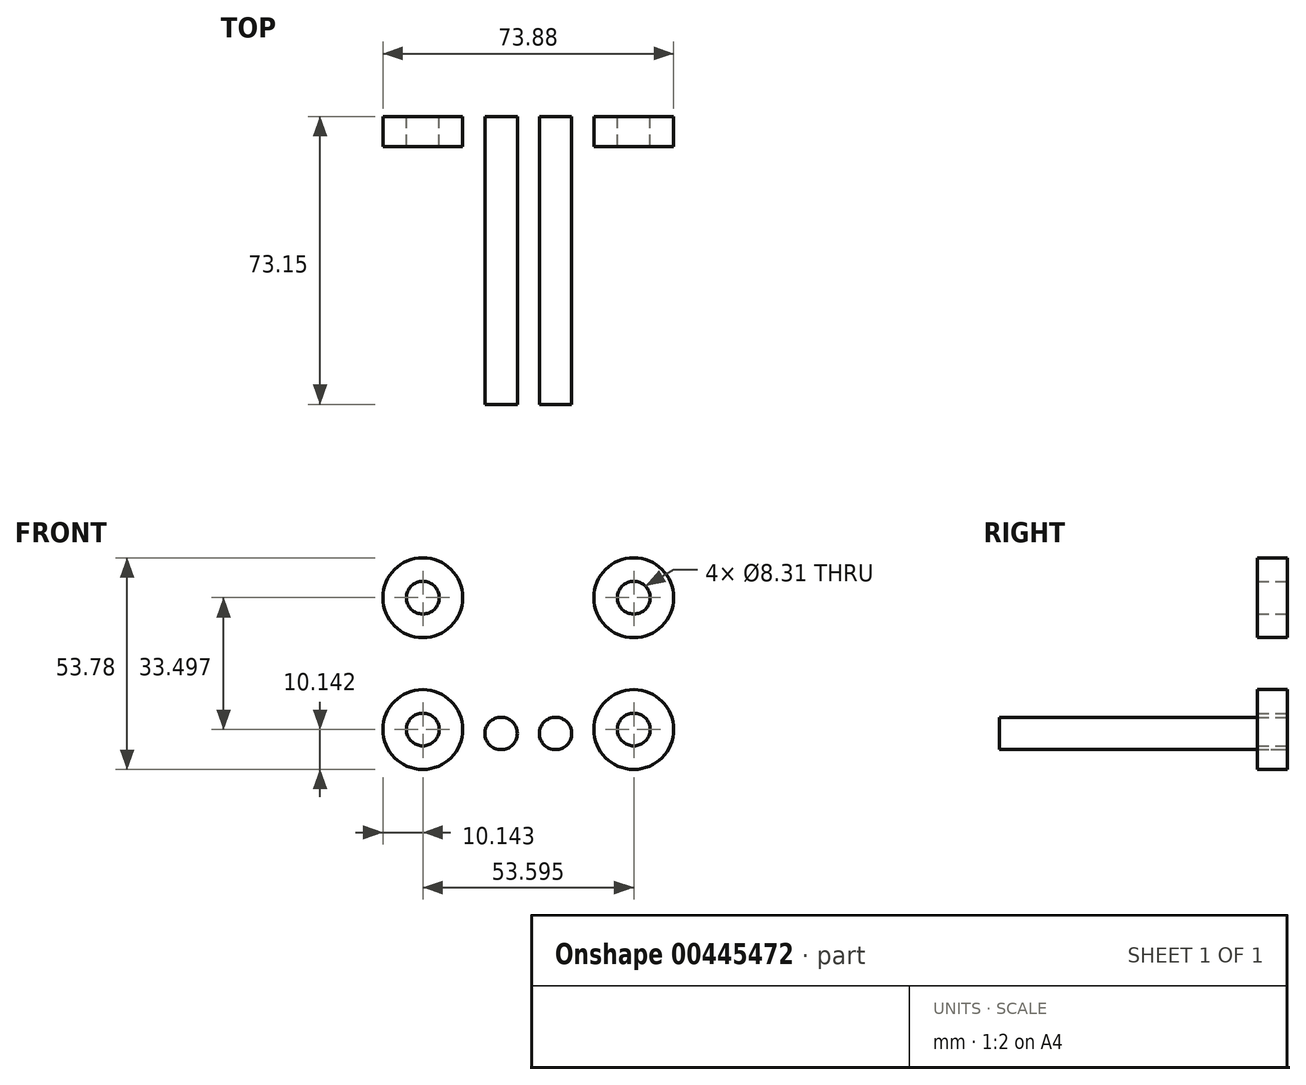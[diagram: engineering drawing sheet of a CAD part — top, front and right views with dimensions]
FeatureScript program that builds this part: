
annotation { "Feature Type Name" : "Feature", "Feature Type Description" : "" }
export const myFeature = defineFeature(function(context is Context, id is Id, definition is map)
    precondition{}
    {
        {
            var Q0;
            Q0=qCreatedBy(makeId("Front.planeOp"),FACE);
            var sketch = newSketch(context, id + "F0", { "sketchPlane" : qUnion([Q0])});
            skCircle(sketch, "E0", {"center": v(-6.92, -17.75) * mm, "radius": 4.11 * mm});
            skCircle(sketch, "E1.MirrorC", {"center": v(6.92, -17.75) * mm, "radius": 4.11 * mm});
            skSolve(sketch);
        }
        {
            var Q0;
            Q0 = qSketchRegion(id + "F0", true);
            extrude(context, id + "F1", {"entities" : qUnion([Q0]), "depth" : 73.15 * mm});
        }
        {
            var Q0;
            Q0=qCreatedBy(makeId("Front.planeOp"),FACE);
            var sketch = newSketch(context, id + "F2", { "sketchPlane" : qUnion([Q0])});
            skCircle(sketch, "E2", {"center": v(-26.8, -16.75) * mm, "radius": 10.14 * mm});
            skCircle(sketch, "E3", {"center": v(-26.8, -16.75) * mm, "radius": 4.15 * mm});
            skCircle(sketch, "E4.MirrorC", {"center": v(26.8, -16.75) * mm, "radius": 10.14 * mm});
            skCircle(sketch, "E5.MirrorC", {"center": v(26.8, -16.75) * mm, "radius": 4.15 * mm});
            skCircle(sketch, "E6.MirrorC", {"center": v(-26.8, 16.75) * mm, "radius": 10.14 * mm});
            skCircle(sketch, "E7.MirrorC", {"center": v(-26.8, 16.75) * mm, "radius": 4.15 * mm});
            skCircle(sketch, "E8.MirrorC", {"center": v(26.8, 16.75) * mm, "radius": 4.15 * mm});
            skCircle(sketch, "E9.MirrorC", {"center": v(26.8, 16.75) * mm, "radius": 10.14 * mm});
            skSolve(sketch);
        }
        {
            var Q0;
            Q0 = qSketchRegion(id + "F2", true);
            extrude(context, id + "F3", {"entities" : qUnion([Q0]), "depth" : 7.62 * mm});
        }
    });
